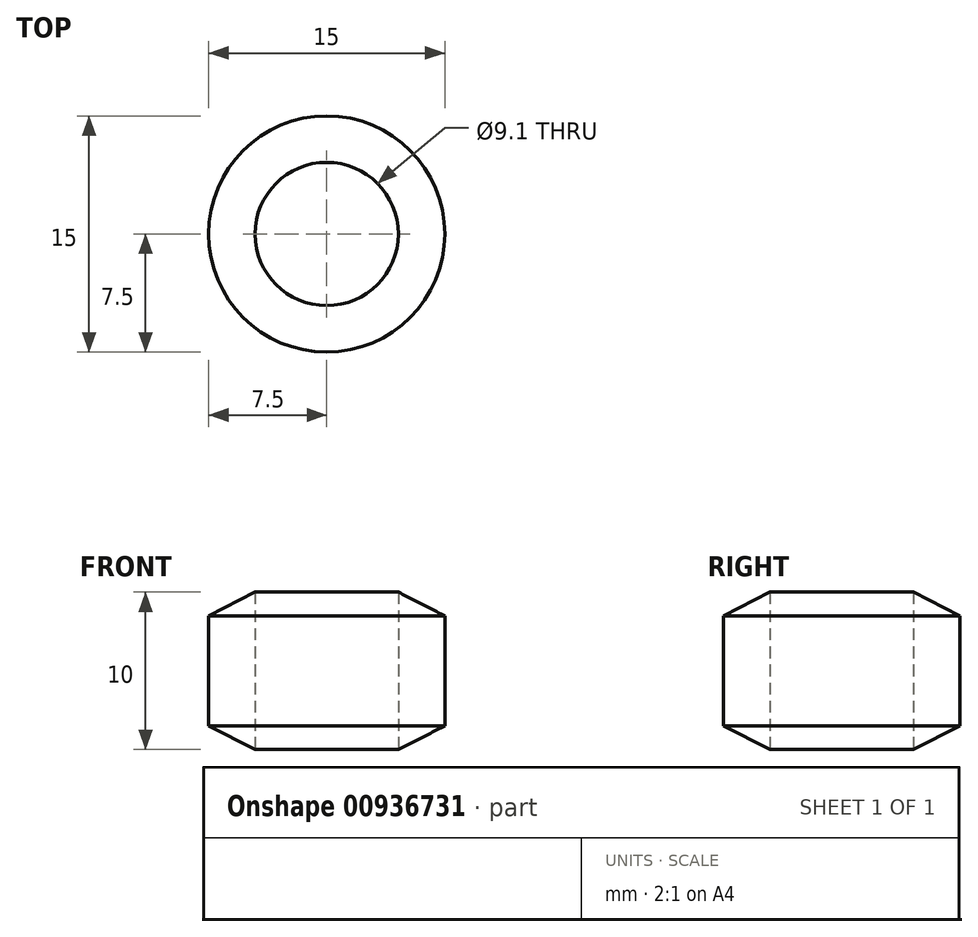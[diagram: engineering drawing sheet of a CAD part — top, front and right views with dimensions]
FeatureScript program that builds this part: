
annotation { "Feature Type Name" : "Feature", "Feature Type Description" : "" }
export const myFeature = defineFeature(function(context is Context, id is Id, definition is map)
    precondition{}
    {
        {
            var Q0;
            Q0=qCreatedBy(makeId("Top.planeOp"),FACE);
            var sketch = newSketch(context, id + "F0", { "sketchPlane" : qUnion([Q0])});
            skCircle(sketch, "E0", {"center": v(0, 0) * mm, "radius": 4.55 * mm});
            skCircle(sketch, "E1", {"center": v(0, 0) * mm, "radius": 7.5 * mm});
            skSolve(sketch);
        }
        {
            var Q0;
            Q0 = qSketchRegion(id + "F0", true);
            var Q1;
            Q1=makeQuery(id+"F0.imprint","IMPRINT",FACE,{"disambiguationData":[TD([[makeQuery(id+"F0.imprint","IMPRINT",EDGE,{"derivedFrom":sQuery(id+"F0.wireOp",EDGE,"E0")}),-1.0]])]});
            extrude(context, id + "F1", {"entities" : qUnion([Q0, Q1]), "depth" : 10 * mm, "offsetDistance" : 25 * mm});
        }
        {
            var Q0;
            Q0=qCreatedBy(makeId("Front.planeOp"),FACE);
            var sketch = newSketch(context, id + "F2", { "sketchPlane" : qUnion([Q0])});
            skPoint(sketch, "E2", {"position": v(7.5, 0) * mm});
            skPoint(sketch, "E3", {"position": v(4.55, 0) * mm});
            skPoint(sketch, "E4", {"position": v(7.5, 1.5) * mm});
            skLineSegment(sketch, "E5", {"start": v(4.55, 0) * mm, "end": v(7.5, 0) * mm});
            skLineSegment(sketch, "E6", {"start": v(4.55, 0) * mm, "end": v(7.5, 1.5) * mm});
            skLineSegment(sketch, "E7", {"start": v(7.5, 0) * mm, "end": v(7.5, 1.5) * mm});
            skSolve(sketch);
        }
        {
            var Q0;
            Q0=qCreatedBy(makeId("Front.planeOp"),FACE);
            var sketch = newSketch(context, id + "F3", { "sketchPlane" : qUnion([Q0])});
            skLineSegment(sketch, "E8", {"start": v(0, 0) * mm, "end": v(0, 59) * mm});
            skSolve(sketch);
        }
        {
            var Q0;
            Q0 = qSketchRegion(id + "F2", true);
            var Q1;
            Q1=sQuery(id+"F3.wireOp",EDGE,"E8");
            revolve(context, id + "F4", {"operationType" : NewBodyOperationType.REMOVE, "surfaceOperationType" : NewSurfaceOperationType.NEW, "entities" : qUnion([Q0]), "axis" : qUnion([Q1]), "revolveType" : RevolveType.FULL, "oppositeDirection" : true});
        }
        {
            var Q0;
            Q0=qCreatedBy(makeId("Front.planeOp"),FACE);
            var sketch = newSketch(context, id + "F5", { "sketchPlane" : qUnion([Q0])});
            skPoint(sketch, "E9", {"position": v(7.5, 10) * mm});
            skPoint(sketch, "E10", {"position": v(4.55, 10) * mm});
            skPoint(sketch, "E11", {"position": v(7.5, 8.5) * mm});
            skLineSegment(sketch, "E12", {"start": v(4.55, 10) * mm, "end": v(7.5, 8.5) * mm});
            skLineSegment(sketch, "E13", {"start": v(7.5, 10) * mm, "end": v(7.5, 8.5) * mm});
            skLineSegment(sketch, "E14", {"start": v(7.5, 10) * mm, "end": v(4.55, 10) * mm});
            skSolve(sketch);
        }
        {
            var Q0;
            Q0 = qSketchRegion(id + "F5", true);
            var Q1;
            Q1=makeQuery(id+"F1.opExtrude","SWEPT_FACE",FACE,{"disambiguationData":[OSD([sQuery(id+"F0.wireOp",EDGE,"E0")])]});
            revolve(context, id + "F6", {"operationType" : NewBodyOperationType.REMOVE, "surfaceOperationType" : NewSurfaceOperationType.NEW, "entities" : qUnion([Q0]), "axis" : qUnion([Q1]), "revolveType" : RevolveType.FULL, "oppositeDirection" : true});
        }
    });
